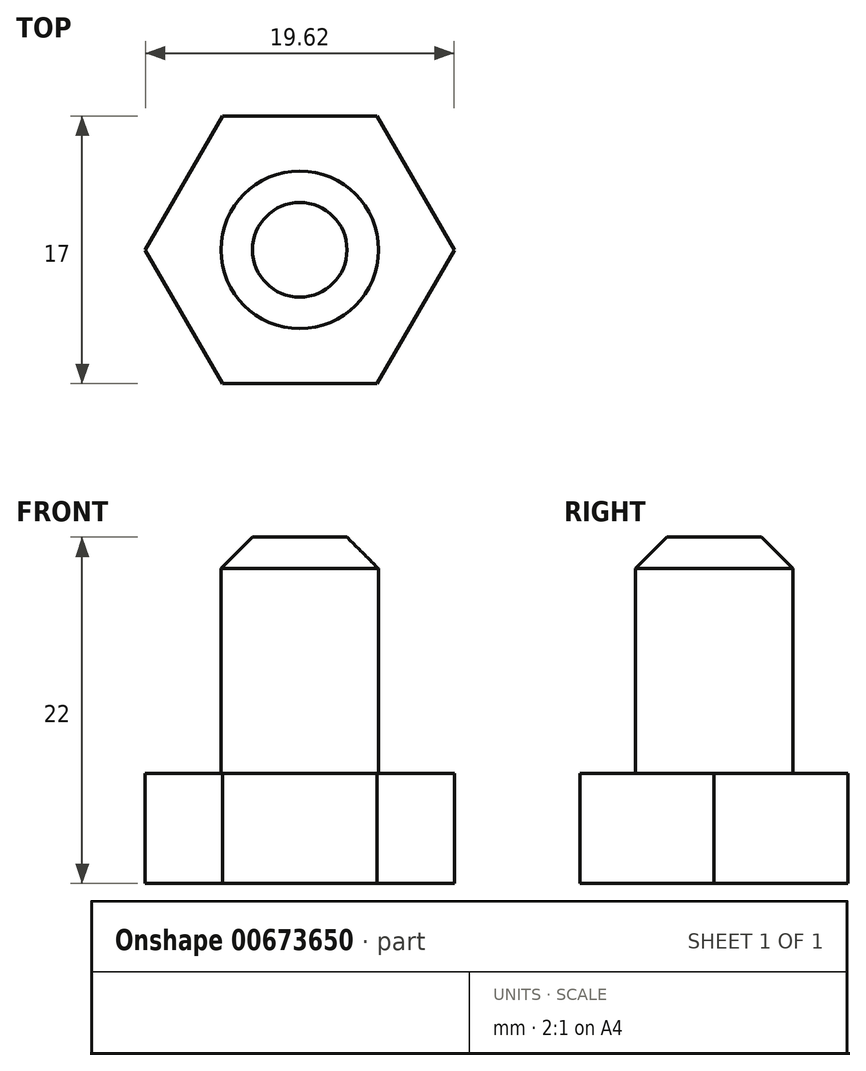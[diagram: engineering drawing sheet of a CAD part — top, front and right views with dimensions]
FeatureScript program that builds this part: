
annotation { "Feature Type Name" : "Feature", "Feature Type Description" : "" }
export const myFeature = defineFeature(function(context is Context, id is Id, definition is map)
    precondition{}
    {
        {
            var Q0;
            Q0=qCreatedBy(makeId("Top.planeOp"),FACE);
            var sketch = newSketch(context, id + "F0", { "sketchPlane" : qUnion([Q0])});
            skCircle(sketch, "E0.cCircle", {"center": v(0, 0) * mm, "radius": 8.5 * mm, "construction": true});
            skLineSegment(sketch, "E0.0", {"start": v(4.9, -8.5) * mm, "end": v(-4.9, -8.5) * mm});
            skLineSegment(sketch, "E0.1", {"start": v(-4.9, -8.5) * mm, "end": v(-9.81, 0) * mm});
            skLineSegment(sketch, "E0.2", {"start": v(-9.81, 0) * mm, "end": v(-4.9, 8.5) * mm});
            skLineSegment(sketch, "E0.3", {"start": v(-4.9, 8.5) * mm, "end": v(4.9, 8.5) * mm});
            skLineSegment(sketch, "E0.4", {"start": v(4.9, 8.5) * mm, "end": v(9.81, 0) * mm});
            skLineSegment(sketch, "E0.5", {"start": v(9.81, 0) * mm, "end": v(4.9, -8.5) * mm});
            skPoint(sketch, "E0.0.midPoint", {"position": v(0, -8.5) * mm});
            skSolve(sketch);
        }
        {
            var Q0;
            Q0 = qSketchRegion(id + "F0", true);
            extrude(context, id + "F1", {"entities" : qUnion([Q0]), "depth" : 7 * mm, "offsetDistance" : 25 * mm});
        }
        {
            var Q0;
            Q0=makeQuery(id+"F1.opExtrude","CAP_FACE",FACE,{"disambiguationData":[OSD([sQuery(id+"F0.wireOp",EDGE,"E0.0"),sQuery(id+"F0.wireOp",EDGE,"E0.1"),sQuery(id+"F0.wireOp",EDGE,"E0.2"),sQuery(id+"F0.wireOp",EDGE,"E0.3"),sQuery(id+"F0.wireOp",EDGE,"E0.4"),sQuery(id+"F0.wireOp",EDGE,"E0.5")])],"isStart":false});
            var sketch = newSketch(context, id + "F2", { "sketchPlane" : qUnion([Q0])});
            skCircle(sketch, "E1", {"center": v(0, 0) * mm, "radius": 5 * mm});
            skSolve(sketch);
        }
        {
            var Q0;
            Q0 = qSketchRegion(id + "F2", true);
            extrude(context, id + "F3", {"entities" : qUnion([Q0]), "operationType" : NewBodyOperationType.ADD, "depth" : 15 * mm, "offsetDistance" : 25 * mm});
        }
        {
            var Q0;
            Q0=makeQuery(id+"F3.opExtrude","CAP_EDGE",EDGE,{"disambiguationData":[OSD([sQuery(id+"F2.wireOp",EDGE,"E1")])],"isStart":false});
            chamfer(context, id + "F4", {"entities" : qUnion([Q0]), "width" : 2 * mm, "tangentPropagation" : true});
        }
    });
